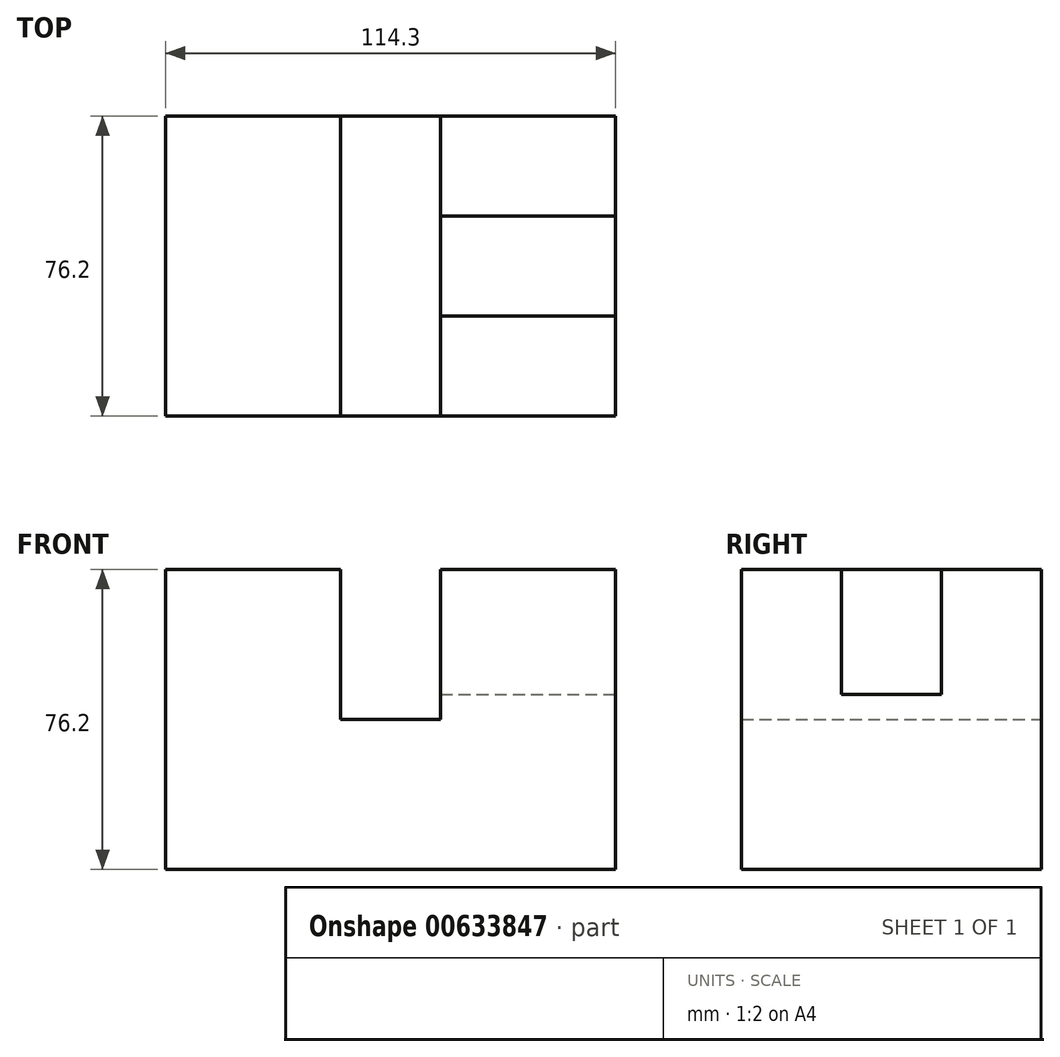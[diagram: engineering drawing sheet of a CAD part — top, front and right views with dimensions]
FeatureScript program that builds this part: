
annotation { "Feature Type Name" : "Feature", "Feature Type Description" : "" }
export const myFeature = defineFeature(function(context is Context, id is Id, definition is map)
    precondition{}
    {
        {
            var Q0;
            Q0=qCreatedBy(makeId("Front.planeOp"),FACE);
            var sketch = newSketch(context, id + "F0", { "sketchPlane" : qUnion([Q0])});
            skLineSegment(sketch, "E0", {"start": v(-59.82, 26.57) * mm, "end": v(-59.82, -49.63) * mm});
            skLineSegment(sketch, "E1", {"start": v(-59.82, -49.63) * mm, "end": v(54.48, -49.63) * mm});
            skLineSegment(sketch, "E2", {"start": v(54.48, -49.63) * mm, "end": v(54.48, 26.57) * mm});
            skLineSegment(sketch, "E3", {"start": v(54.48, 26.57) * mm, "end": v(10.03, 26.57) * mm});
            skLineSegment(sketch, "E4", {"start": v(10.03, 26.57) * mm, "end": v(10.03, -11.53) * mm});
            skLineSegment(sketch, "E5", {"start": v(10.03, -11.53) * mm, "end": v(-15.37, -11.53) * mm});
            skLineSegment(sketch, "E6", {"start": v(-15.37, -11.53) * mm, "end": v(-15.37, 26.57) * mm});
            skLineSegment(sketch, "E7", {"start": v(-15.37, 26.57) * mm, "end": v(-59.82, 26.57) * mm});
            skSolve(sketch);
        }
        {
            var Q0;
            Q0=makeQuery(id+"F0.imprint","IMPRINT",FACE,{"disambiguationData":[TD([[makeQuery(id+"F0.imprint","IMPRINT",EDGE,{"derivedFrom":sQuery(id+"F0.wireOp",EDGE,"E0")}),1.0]])]});
            extrude(context, id + "F1", {"entities" : qUnion([Q0]), "depth" : 76.2 * mm, "offsetDistance" : 25.4 * mm});
        }
        {
            var Q0;
            Q0=makeQuery(id+"F1.opExtrude","SWEPT_FACE",FACE,{"disambiguationData":[OSD([sQuery(id+"F0.wireOp",EDGE,"E3")])]});
            var sketch = newSketch(context, id + "F2", { "sketchPlane" : qUnion([Q0])});
            skLineSegment(sketch, "E8", {"start": v(10.03, -25.4) * mm, "end": v(54.48, -25.4) * mm});
            skLineSegment(sketch, "E9", {"start": v(10.03, -50.8) * mm, "end": v(54.48, -50.8) * mm});
            skSolve(sketch);
        }
        {
            var Q0;
            {var subQ0=sQuery(id+"F2.wireOp",EDGE,"E8");Q0=makeQuery(id+"F2.imprint","IMPRINT",FACE,{"disambiguationData":[TD([[makeQuery(id+"F2.imprint","IMPRINT",EDGE,{"derivedFrom":subQ0}),-1.0]])]});}
            extrude(context, id + "F3", {"entities" : qUnion([Q0]), "operationType" : NewBodyOperationType.REMOVE, "oppositeDirection" : true, "depth" : 31.75 * mm, "offsetDistance" : 25.4 * mm});
        }
    });
